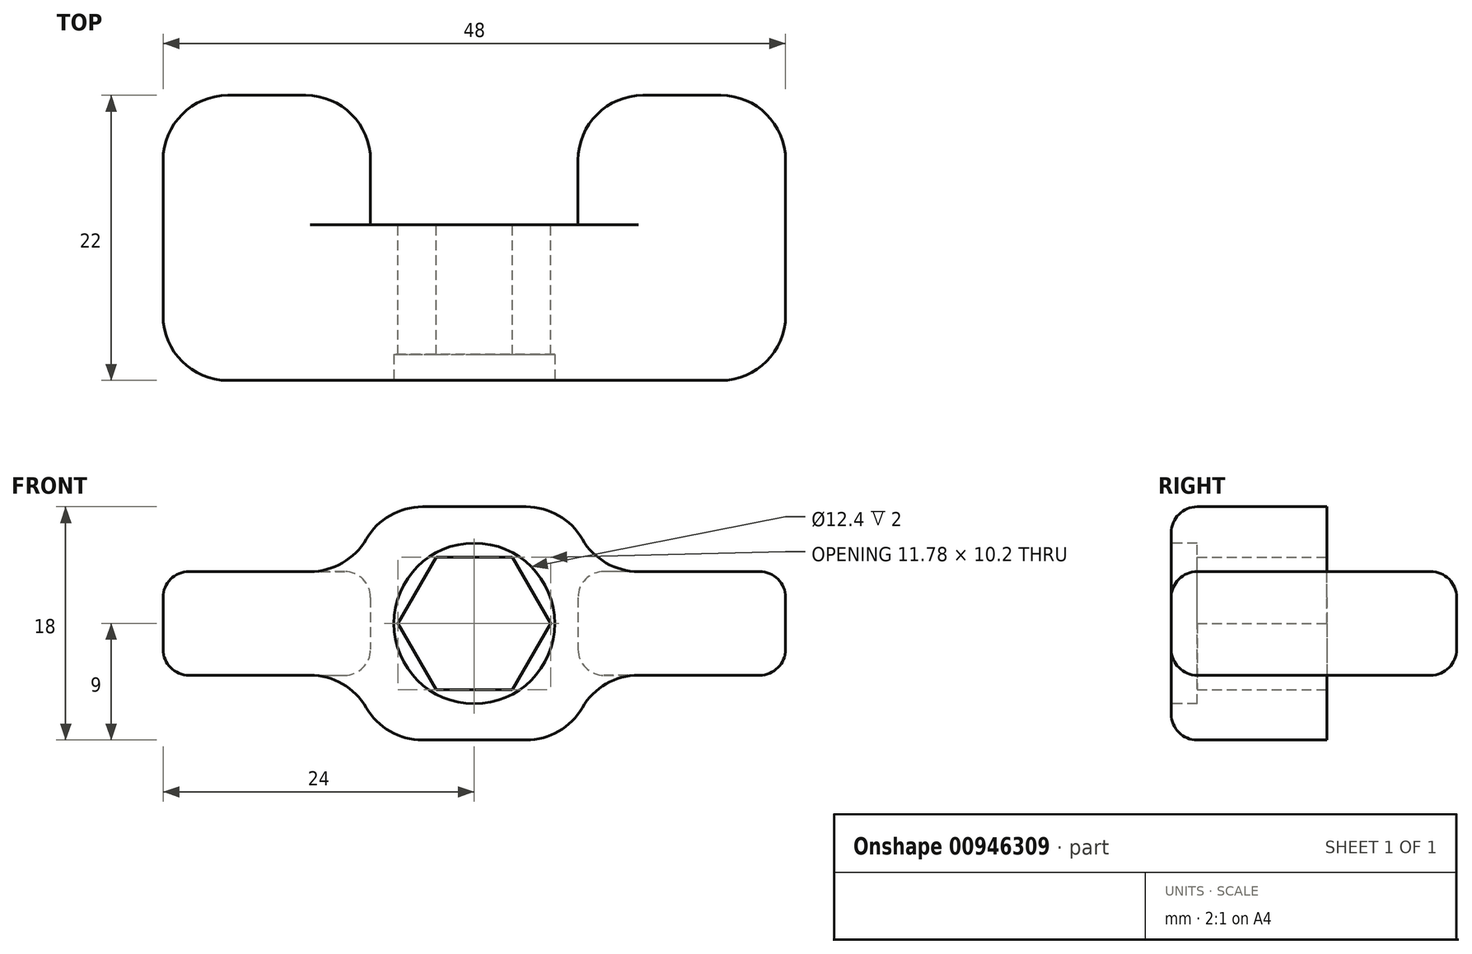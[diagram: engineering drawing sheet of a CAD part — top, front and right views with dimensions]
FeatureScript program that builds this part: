
annotation { "Feature Type Name" : "Feature", "Feature Type Description" : "" }
export const myFeature = defineFeature(function(context is Context, id is Id, definition is map)
    precondition{}
    {
        {
            var Q0;
            Q0=qCreatedBy(makeId("Front.planeOp"),FACE);
            var sketch = newSketch(context, id + "F0", { "sketchPlane" : qUnion([Q0])});
            skLineSegment(sketch, "E0.bottom", {"start": v(9, -9) * mm, "end": v(-9, -9) * mm});
            skLineSegment(sketch, "E0.top", {"start": v(9, 9) * mm, "end": v(-9, 9) * mm});
            skLineSegment(sketch, "E0.left", {"start": v(9, -9) * mm, "end": v(9, 9) * mm});
            skLineSegment(sketch, "E0.right", {"start": v(-9, -9) * mm, "end": v(-9, 9) * mm});
            skPoint(sketch, "E0.middle", {"position": v(0, 0) * mm});
            skCircle(sketch, "E1.cCircle", {"center": v(0, 0) * mm, "radius": 5.1 * mm, "construction": true});
            skLineSegment(sketch, "E1.0", {"start": v(-2.94, 5.1) * mm, "end": v(2.94, 5.1) * mm});
            skLineSegment(sketch, "E1.1", {"start": v(2.94, 5.1) * mm, "end": v(5.89, 0) * mm});
            skLineSegment(sketch, "E1.2", {"start": v(5.89, 0) * mm, "end": v(2.94, -5.1) * mm});
            skLineSegment(sketch, "E1.3", {"start": v(2.94, -5.1) * mm, "end": v(-2.94, -5.1) * mm});
            skLineSegment(sketch, "E1.4", {"start": v(-2.94, -5.1) * mm, "end": v(-5.89, 0) * mm});
            skLineSegment(sketch, "E1.5", {"start": v(-5.89, 0) * mm, "end": v(-2.94, 5.1) * mm});
            skPoint(sketch, "E1.0.midPoint", {"position": v(0, 5.1) * mm});
            skLineSegment(sketch, "E2.bottom", {"start": v(9, 4) * mm, "end": v(24, 4) * mm});
            skLineSegment(sketch, "E2.top", {"start": v(9, -4) * mm, "end": v(24, -4) * mm});
            skLineSegment(sketch, "E2.left", {"start": v(9, 4) * mm, "end": v(9, -4) * mm});
            skLineSegment(sketch, "E2.right", {"start": v(24, 4) * mm, "end": v(24, -4) * mm});
            skLineSegment(sketch, "E3", {"start": v(-33.64, 0) * mm, "end": v(32.8, 0) * mm, "construction": true});
            skPoint(sketch, "E3.endSnap0", {"position": v(9, 0) * mm});
            skLineSegment(sketch, "E4", {"start": v(0, 19.03) * mm, "end": v(0, -17.7) * mm, "construction": true});
            skPoint(sketch, "E4.endSnap0", {"position": v(0, -9) * mm});
            skLineSegment(sketch, "E5.MirrorCS", {"start": v(-9, 4) * mm, "end": v(-24, 4) * mm});
            skLineSegment(sketch, "E6.MirrorCS", {"start": v(-24, 4) * mm, "end": v(-24, -4) * mm});
            skLineSegment(sketch, "E7.MirrorCS", {"start": v(-9, -4) * mm, "end": v(-24, -4) * mm});
            skSolve(sketch);
        }
        {
            var Q0;
            {var subQ2=sQuery(id+"F0.wireOp",EDGE,"E5.MirrorCS");Q0=makeQuery(id+"F0.imprint","IMPRINT",FACE,{"disambiguationData":[TD([[makeQuery(id+"F0.imprint","IMPRINT",EDGE,{"derivedFrom":subQ2}),1.0]])]});}
            var Q1;
            {var subQ1=sQuery(id+"F0.wireOp",EDGE,"E0.bottom");Q1=makeQuery(id+"F0.imprint","IMPRINT",FACE,{"disambiguationData":[TD([[makeQuery(id+"F0.imprint","IMPRINT",EDGE,{"derivedFrom":subQ1}),-1.0]])]});}
            var Q2;
            {var subQ2=sQuery(id+"F0.wireOp",EDGE,"E2.bottom");Q2=makeQuery(id+"F0.imprint","IMPRINT",FACE,{"disambiguationData":[TD([[makeQuery(id+"F0.imprint","IMPRINT",EDGE,{"derivedFrom":subQ2}),-1.0]])]});}
            extrude(context, id + "F1", {"entities" : qUnion([Q0, Q1, Q2]), "depth" : 12 * mm, "offsetDistance" : 25 * mm});
        }
        {
            var Q0;
            Q0=makeQuery(id+"F1.opExtrude","SWEPT_EDGE",EDGE,{"disambiguationData":[OSD([sQuery(id+"F0.wireOp",EDGE,"E0.top"),sQuery(id+"F0.wireOp",EDGE,"E0.left")])]});
            var Q1;
            Q1=makeQuery(id+"F1.opExtrude","SWEPT_EDGE",EDGE,{"disambiguationData":[OSD([sQuery(id+"F0.wireOp",EDGE,"E0.bottom"),sQuery(id+"F0.wireOp",EDGE,"E0.left")])]});
            var Q2;
            Q2=makeQuery(id+"F1.opExtrude","SWEPT_EDGE",EDGE,{"disambiguationData":[OSD([sQuery(id+"F0.wireOp",EDGE,"E0.bottom"),sQuery(id+"F0.wireOp",EDGE,"E0.right")])]});
            var Q3;
            Q3=makeQuery(id+"F1.opExtrude","SWEPT_EDGE",EDGE,{"disambiguationData":[OSD([sQuery(id+"F0.wireOp",EDGE,"E0.top"),sQuery(id+"F0.wireOp",EDGE,"E0.right")])]});
            fillet(context, id + "F2", {"entities" : qUnion([Q0, Q1, Q2, Q3]), "radius" : 5 * mm, "tangentPropagation" : true, "allowEdgeOverflow" : false});
        }
        {
            var Q0;
            Q0=makeQuery(id+"F2.opFillet","BLEND_EDGE",EDGE,{"blendedFrom":[makeQuery(id+"F1.opExtrude","SWEPT_EDGE",EDGE,{"disambiguationData":[OSD([sQuery(id+"F0.wireOp",EDGE,"E0.bottom"),sQuery(id+"F0.wireOp",EDGE,"E0.left")])]}),makeQuery(id+"F1.opExtrude","SWEPT_FACE",FACE,{"disambiguationData":[OSD([sQuery(id+"F0.wireOp",EDGE,"E2.top")])]})],"blendedInto":[makeQuery(id+"F1.opExtrude","SWEPT_FACE",FACE,{"disambiguationData":[OSD([sQuery(id+"F0.wireOp",EDGE,"E2.top")])]})]});
            var Q1;
            Q1=makeQuery(id+"F2.opFillet","BLEND_EDGE",EDGE,{"blendedFrom":[makeQuery(id+"F1.opExtrude","SWEPT_EDGE",EDGE,{"disambiguationData":[OSD([sQuery(id+"F0.wireOp",EDGE,"E0.bottom"),sQuery(id+"F0.wireOp",EDGE,"E0.right")])]}),makeQuery(id+"F1.opExtrude","SWEPT_FACE",FACE,{"disambiguationData":[OSD([sQuery(id+"F0.wireOp",EDGE,"E7.MirrorCS")])]})],"blendedInto":[makeQuery(id+"F1.opExtrude","SWEPT_FACE",FACE,{"disambiguationData":[OSD([sQuery(id+"F0.wireOp",EDGE,"E7.MirrorCS")])]})]});
            var Q2;
            Q2=makeQuery(id+"F2.opFillet","BLEND_EDGE",EDGE,{"blendedFrom":[makeQuery(id+"F1.opExtrude","SWEPT_EDGE",EDGE,{"disambiguationData":[OSD([sQuery(id+"F0.wireOp",EDGE,"E0.top"),sQuery(id+"F0.wireOp",EDGE,"E0.right")])]}),makeQuery(id+"F1.opExtrude","SWEPT_FACE",FACE,{"disambiguationData":[OSD([sQuery(id+"F0.wireOp",EDGE,"E5.MirrorCS")])]})],"blendedInto":[makeQuery(id+"F1.opExtrude","SWEPT_FACE",FACE,{"disambiguationData":[OSD([sQuery(id+"F0.wireOp",EDGE,"E5.MirrorCS")])]})]});
            var Q3;
            Q3=makeQuery(id+"F2.opFillet","BLEND_EDGE",EDGE,{"blendedFrom":[makeQuery(id+"F1.opExtrude","SWEPT_EDGE",EDGE,{"disambiguationData":[OSD([sQuery(id+"F0.wireOp",EDGE,"E0.top"),sQuery(id+"F0.wireOp",EDGE,"E0.left")])]}),makeQuery(id+"F1.opExtrude","SWEPT_FACE",FACE,{"disambiguationData":[OSD([sQuery(id+"F0.wireOp",EDGE,"E2.bottom")])]})],"blendedInto":[makeQuery(id+"F1.opExtrude","SWEPT_FACE",FACE,{"disambiguationData":[OSD([sQuery(id+"F0.wireOp",EDGE,"E2.bottom")])]})]});
            fillet(context, id + "F3", {"entities" : qUnion([Q0, Q1, Q2, Q3]), "radius" : 5 * mm, "tangentPropagation" : true, "allowEdgeOverflow" : false});
        }
        {
            var Q0;
            Q0=makeQuery(id+"F1.opExtrude","CAP_FACE",FACE,{"disambiguationData":[OSD([sQuery(id+"F0.wireOp",EDGE,"E0.bottom"),sQuery(id+"F0.wireOp",EDGE,"E0.top"),sQuery(id+"F0.wireOp",EDGE,"E0.left"),sQuery(id+"F0.wireOp",EDGE,"E0.right"),sQuery(id+"F0.wireOp",EDGE,"E1.0"),sQuery(id+"F0.wireOp",EDGE,"E1.1"),sQuery(id+"F0.wireOp",EDGE,"E1.2"),sQuery(id+"F0.wireOp",EDGE,"E1.3"),sQuery(id+"F0.wireOp",EDGE,"E1.4"),sQuery(id+"F0.wireOp",EDGE,"E1.5"),sQuery(id+"F0.wireOp",EDGE,"E2.bottom"),sQuery(id+"F0.wireOp",EDGE,"E2.top"),sQuery(id+"F0.wireOp",EDGE,"E2.right"),sQuery(id+"F0.wireOp",EDGE,"E5.MirrorCS"),sQuery(id+"F0.wireOp",EDGE,"E6.MirrorCS"),sQuery(id+"F0.wireOp",EDGE,"E7.MirrorCS")])],"isStart":true});
            var sketch = newSketch(context, id + "F4", { "sketchPlane" : qUnion([Q0])});
            skLineSegment(sketch, "E8.bottom", {"start": v(-24, 4) * mm, "end": v(-8, 4) * mm});
            skLineSegment(sketch, "E8.top", {"start": v(-24, -4) * mm, "end": v(-8, -4) * mm});
            skLineSegment(sketch, "E8.left", {"start": v(-24, 4) * mm, "end": v(-24, -4) * mm});
            skLineSegment(sketch, "E8.right", {"start": v(-8, 4) * mm, "end": v(-8, -4) * mm});
            skLineSegment(sketch, "E9.bottom", {"start": v(24, 4) * mm, "end": v(8, 4) * mm});
            skLineSegment(sketch, "E9.top", {"start": v(24, -4) * mm, "end": v(8, -4) * mm});
            skLineSegment(sketch, "E9.left", {"start": v(24, 4) * mm, "end": v(24, -4) * mm});
            skLineSegment(sketch, "E9.right", {"start": v(8, 4) * mm, "end": v(8, -4) * mm});
            skSolve(sketch);
        }
        {
            var Q0;
            {var subQ9=sQuery(id+"F4.wireOp",EDGE,"E8.left");Q0=makeQuery(id+"F4.imprint","IMPRINT",FACE,{"disambiguationData":[TD([[makeQuery(id+"F4.imprint","IMPRINT",EDGE,{"derivedFrom":subQ9}),1.0]])]});}
            var Q1;
            {var subQ9=sQuery(id+"F4.wireOp",EDGE,"E9.left");Q1=makeQuery(id+"F4.imprint","IMPRINT",FACE,{"disambiguationData":[TD([[makeQuery(id+"F4.imprint","IMPRINT",EDGE,{"derivedFrom":subQ9}),-1.0]])]});}
            extrude(context, id + "F5", {"entities" : qUnion([Q0, Q1]), "operationType" : NewBodyOperationType.ADD, "depth" : 10 * mm, "offsetDistance" : 25 * mm});
        }
        {
            var Q0;
            Q0=makeQuery(id+"F5.opExtrude","CAP_EDGE",EDGE,{"disambiguationData":[OSD([sQuery(id+"F4.wireOp",EDGE,"E9.left")])],"isStart":false});
            var Q1;
            Q1=makeQuery(id+"F5.opExtrude","CAP_EDGE",EDGE,{"disambiguationData":[OSD([sQuery(id+"F4.wireOp",EDGE,"E8.left")])],"isStart":false});
            var Q2;
            Q2=makeQuery(id+"F5.opExtrude","CAP_EDGE",EDGE,{"disambiguationData":[OSD([sQuery(id+"F4.wireOp",EDGE,"E8.right")])],"isStart":false});
            var Q3;
            Q3=makeQuery(id+"F5.opExtrude","CAP_EDGE",EDGE,{"disambiguationData":[OSD([sQuery(id+"F4.wireOp",EDGE,"E9.right")])],"isStart":false});
            var Q4;
            Q4=makeQuery(id+"F1.opExtrude","CAP_EDGE",EDGE,{"disambiguationData":[OSD([sQuery(id+"F0.wireOp",EDGE,"E6.MirrorCS")])],"isStart":false});
            var Q5;
            Q5=makeQuery(id+"F1.opExtrude","CAP_EDGE",EDGE,{"disambiguationData":[OSD([sQuery(id+"F0.wireOp",EDGE,"E2.right")])],"isStart":false});
            fillet(context, id + "F6", {"entities" : qUnion([Q0, Q1, Q2, Q3, Q4, Q5]), "radius" : 5 * mm, "tangentPropagation" : true, "allowEdgeOverflow" : false});
        }
        {
            var Q0;
            Q0=makeQuery(id+"F5.opExtrude","CAP_EDGE",EDGE,{"disambiguationData":[OSD([sQuery(id+"F4.wireOp",EDGE,"E9.bottom")])],"isStart":false});
            var Q1;
            Q1=makeQuery(id+"F6.opFillet","BLEND_EDGE",EDGE,{"blendedFrom":[makeQuery(id+"F5.opExtrude","CAP_EDGE",EDGE,{"disambiguationData":[OSD([sQuery(id+"F4.wireOp",EDGE,"E9.left")])],"isStart":false}),makeQuery(id+"F5.boolean.opBoolean","MERGE",FACE,{"derivedFrom":[makeQuery(id+"F1.opExtrude","SWEPT_FACE",FACE,{"disambiguationData":[OSD([sQuery(id+"F0.wireOp",EDGE,"E5.MirrorCS")])]}),makeQuery(id+"F5.opExtrude","SWEPT_FACE",FACE,{"disambiguationData":[OSD([sQuery(id+"F4.wireOp",EDGE,"E9.bottom")])]})]})],"blendedInto":[makeQuery(id+"F5.boolean.opBoolean","MERGE",FACE,{"derivedFrom":[makeQuery(id+"F1.opExtrude","SWEPT_FACE",FACE,{"disambiguationData":[OSD([sQuery(id+"F0.wireOp",EDGE,"E5.MirrorCS")])]}),makeQuery(id+"F5.opExtrude","SWEPT_FACE",FACE,{"disambiguationData":[OSD([sQuery(id+"F4.wireOp",EDGE,"E9.bottom")])]})]})]});
            var Q2;
            Q2=makeQuery(id+"F6.opFillet","BLEND_EDGE",EDGE,{"blendedFrom":[makeQuery(id+"F5.opExtrude","CAP_EDGE",EDGE,{"disambiguationData":[OSD([sQuery(id+"F4.wireOp",EDGE,"E9.right")])],"isStart":false}),makeQuery(id+"F5.boolean.opBoolean","MERGE",FACE,{"derivedFrom":[makeQuery(id+"F1.opExtrude","SWEPT_FACE",FACE,{"disambiguationData":[OSD([sQuery(id+"F0.wireOp",EDGE,"E5.MirrorCS")])]}),makeQuery(id+"F5.opExtrude","SWEPT_FACE",FACE,{"disambiguationData":[OSD([sQuery(id+"F4.wireOp",EDGE,"E9.bottom")])]})]})],"blendedInto":[makeQuery(id+"F5.boolean.opBoolean","MERGE",FACE,{"derivedFrom":[makeQuery(id+"F1.opExtrude","SWEPT_FACE",FACE,{"disambiguationData":[OSD([sQuery(id+"F0.wireOp",EDGE,"E5.MirrorCS")])]}),makeQuery(id+"F5.opExtrude","SWEPT_FACE",FACE,{"disambiguationData":[OSD([sQuery(id+"F4.wireOp",EDGE,"E9.bottom")])]})]})]});
            var Q3;
            Q3=makeQuery(id+"F5.opExtrude","CAP_EDGE",EDGE,{"disambiguationData":[OSD([sQuery(id+"F4.wireOp",EDGE,"E9.top")])],"isStart":false});
            fillet(context, id + "F7", {"entities" : qUnion([Q0, Q1, Q2, Q3]), "radius" : 2 * mm, "tangentPropagation" : true, "allowEdgeOverflow" : false});
        }
        {
            var Q0;
            Q0=makeQuery(id+"F1.opExtrude","CAP_FACE",FACE,{"disambiguationData":[OSD([sQuery(id+"F0.wireOp",EDGE,"E0.bottom"),sQuery(id+"F0.wireOp",EDGE,"E0.top"),sQuery(id+"F0.wireOp",EDGE,"E0.left"),sQuery(id+"F0.wireOp",EDGE,"E0.right"),sQuery(id+"F0.wireOp",EDGE,"E1.0"),sQuery(id+"F0.wireOp",EDGE,"E1.1"),sQuery(id+"F0.wireOp",EDGE,"E1.2"),sQuery(id+"F0.wireOp",EDGE,"E1.3"),sQuery(id+"F0.wireOp",EDGE,"E1.4"),sQuery(id+"F0.wireOp",EDGE,"E1.5"),sQuery(id+"F0.wireOp",EDGE,"E2.bottom"),sQuery(id+"F0.wireOp",EDGE,"E2.top"),sQuery(id+"F0.wireOp",EDGE,"E2.right"),sQuery(id+"F0.wireOp",EDGE,"E5.MirrorCS"),sQuery(id+"F0.wireOp",EDGE,"E6.MirrorCS"),sQuery(id+"F0.wireOp",EDGE,"E7.MirrorCS")])],"isStart":false});
            var sketch = newSketch(context, id + "F8", { "sketchPlane" : qUnion([Q0])});
            skCircle(sketch, "E10", {"center": v(0, 0) * mm, "radius": 6.2 * mm});
            skSolve(sketch);
        }
        {
            var Q0;
            Q0=makeQuery(id+"F8.imprint","IMPRINT",FACE,{"disambiguationData":[TD([[makeQuery(id+"F8.imprint","IMPRINT",EDGE,{"derivedFrom":sQuery(id+"F8.wireOp",EDGE,"E10")}),1.0]])]});
            extrude(context, id + "F9", {"entities" : qUnion([Q0]), "operationType" : NewBodyOperationType.REMOVE, "oppositeDirection" : true, "depth" : 2 * mm, "offsetDistance" : 25 * mm});
        }
    });
